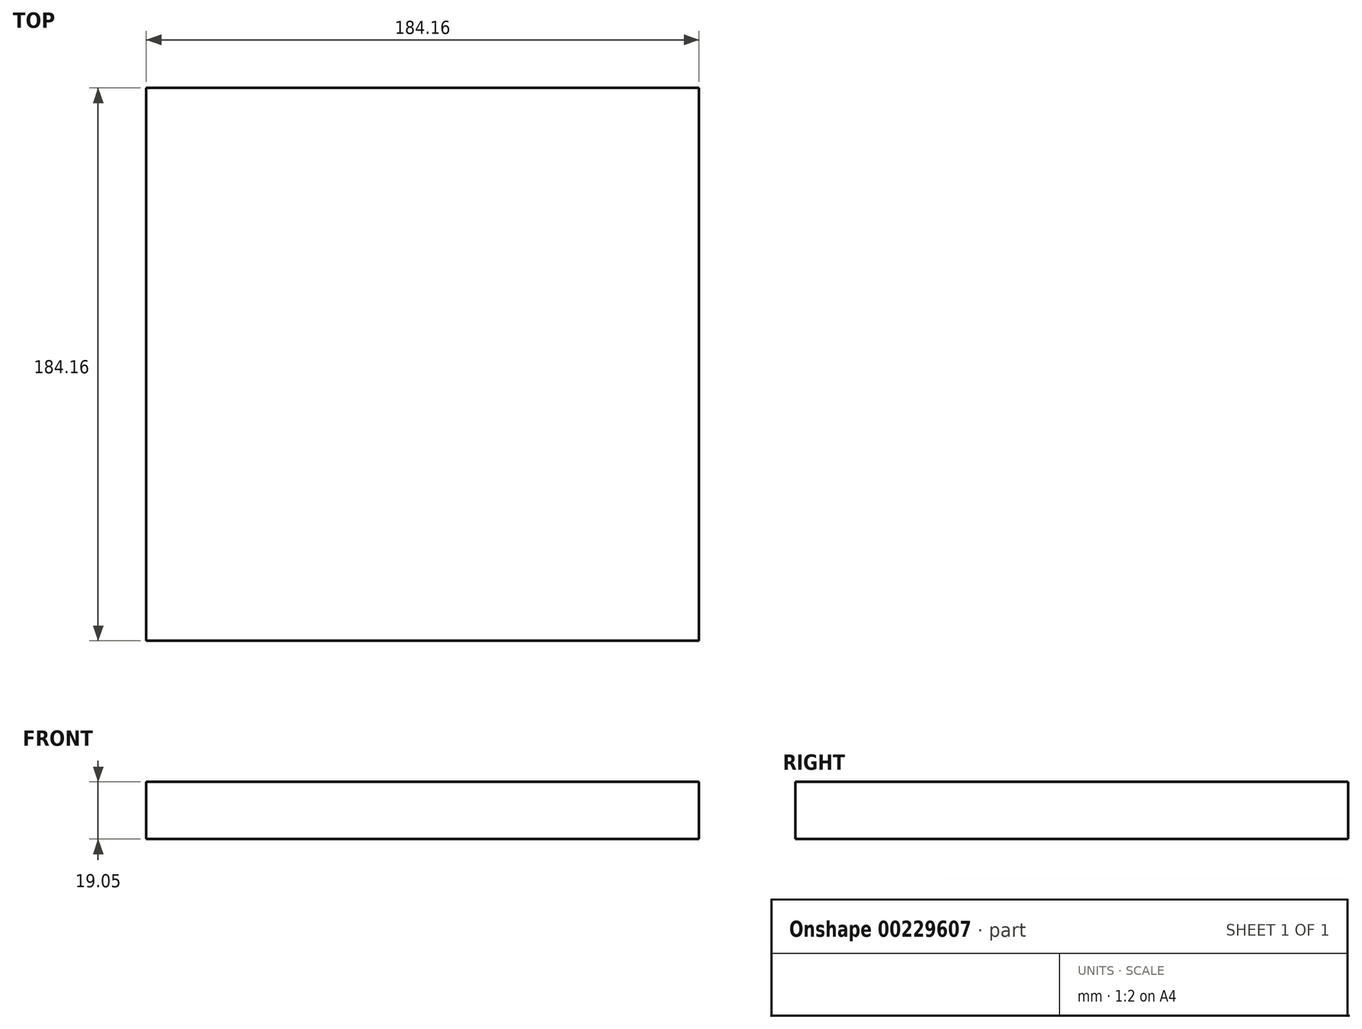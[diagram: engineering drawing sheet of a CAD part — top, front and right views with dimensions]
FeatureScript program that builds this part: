
annotation { "Feature Type Name" : "Feature", "Feature Type Description" : "" }
export const myFeature = defineFeature(function(context is Context, id is Id, definition is map)
    precondition{}
    {
        {
            var Q0;
            Q0=qCreatedBy(makeId("Top.planeOp"),FACE);
            var sketch = newSketch(context, id + "F0", { "sketchPlane" : qUnion([Q0])});
            skLineSegment(sketch, "E0.bottom", {"start": v(92.08, -92.07) * mm, "end": v(-92.07, -92.07) * mm});
            skLineSegment(sketch, "E0.top", {"start": v(92.07, 92.07) * mm, "end": v(-92.08, 92.07) * mm});
            skLineSegment(sketch, "E0.left", {"start": v(92.08, -92.07) * mm, "end": v(92.08, 92.08) * mm});
            skLineSegment(sketch, "E0.right", {"start": v(-92.07, -92.07) * mm, "end": v(-92.08, 92.08) * mm});
            skPoint(sketch, "E0.middle", {"position": v(0, 0) * mm});
            skSolve(sketch);
        }
        {
            var Q0;
            Q0 = qSketchRegion(id + "F0", true);
            extrude(context, id + "F1", {"entities" : qUnion([Q0]), "depth" : 19.05 * mm});
        }
    });
